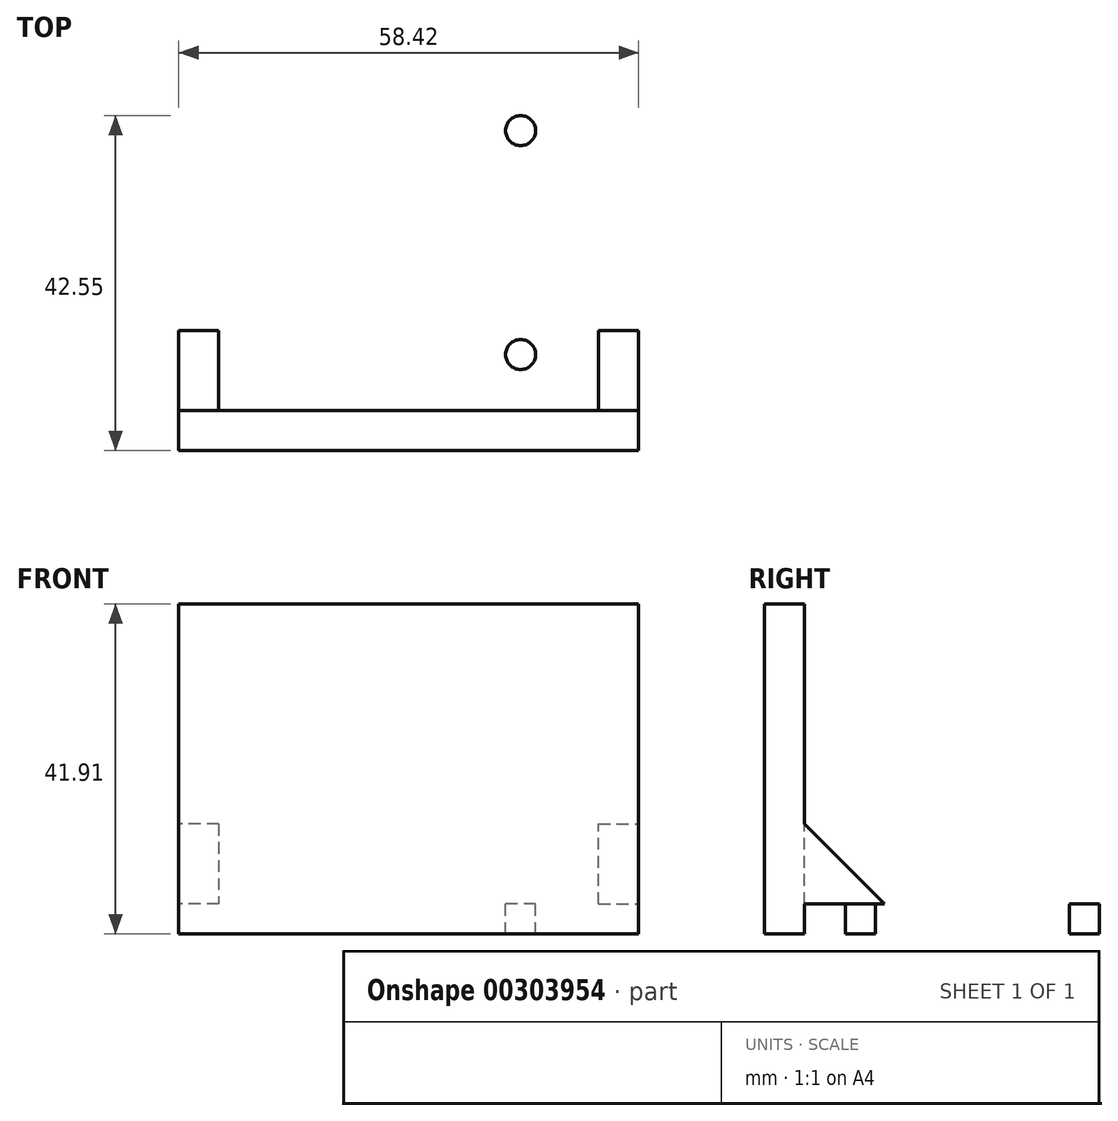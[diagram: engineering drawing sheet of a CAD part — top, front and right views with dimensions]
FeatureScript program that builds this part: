
annotation { "Feature Type Name" : "Feature", "Feature Type Description" : "" }
export const myFeature = defineFeature(function(context is Context, id is Id, definition is map)
    precondition{}
    {
        {
            var Q0;
            Q0=qCreatedBy(makeId("Top.planeOp"),FACE);
            var sketch = newSketch(context, id + "F0", { "sketchPlane" : qUnion([Q0])});
            skLineSegment(sketch, "E0.bottom", {"start": v(29.21, 22.86) * mm, "end": v(-29.21, 22.86) * mm});
            skLineSegment(sketch, "E0.top", {"start": v(29.21, -22.86) * mm, "end": v(-29.21, -22.86) * mm});
            skLineSegment(sketch, "E0.left", {"start": v(29.21, 22.86) * mm, "end": v(29.21, -22.86) * mm});
            skLineSegment(sketch, "E0.right", {"start": v(-29.21, 22.86) * mm, "end": v(-29.21, -22.86) * mm});
            skPoint(sketch, "E0.middle", {"position": v(0, 0) * mm});
            skSolve(sketch);
        }
        {
            var Q0;
            Q0 = qSketchRegion(id + "F0", true);
            extrude(context, id + "F1", {"entities" : qUnion([Q0]), "depth" : 3.8 * mm});
        }
        {
            var Q0;
            Q0=makeQuery(id+"F1.opExtrude","CAP_FACE",FACE,{"disambiguationData":[OSD([sQuery(id+"F0.wireOp",EDGE,"E0.bottom"),sQuery(id+"F0.wireOp",EDGE,"E0.top"),sQuery(id+"F0.wireOp",EDGE,"E0.left"),sQuery(id+"F0.wireOp",EDGE,"E0.right")])],"isStart":false});
            var sketch = newSketch(context, id + "F2", { "sketchPlane" : qUnion([Q0])});
            skLineSegment(sketch, "E1.bottom", {"start": v(-29.21, -22.86) * mm, "end": v(29.21, -22.86) * mm});
            skLineSegment(sketch, "E1.top", {"start": v(-29.21, -17.78) * mm, "end": v(29.21, -17.78) * mm});
            skLineSegment(sketch, "E1.left", {"start": v(-29.21, -22.86) * mm, "end": v(-29.21, -17.78) * mm});
            skLineSegment(sketch, "E1.right", {"start": v(29.21, -22.86) * mm, "end": v(29.21, -17.78) * mm});
            skSolve(sketch);
        }
        {
            var Q0;
            Q0 = qSketchRegion(id + "F2", true);
            extrude(context, id + "F3", {"entities" : qUnion([Q0]), "operationType" : NewBodyOperationType.ADD, "depth" : 38.1 * mm});
        }
        {
            var Q0;
            Q0=makeQuery(id+"F1.opExtrude","CAP_FACE",FACE,{"disambiguationData":[OSD([sQuery(id+"F0.wireOp",EDGE,"E0.bottom"),sQuery(id+"F0.wireOp",EDGE,"E0.top"),sQuery(id+"F0.wireOp",EDGE,"E0.left"),sQuery(id+"F0.wireOp",EDGE,"E0.right")])],"isStart":false});
            var sketch = newSketch(context, id + "F4", { "sketchPlane" : qUnion([Q0])});
            skCircle(sketch, "E2", {"center": v(-14.22, 17.78) * mm, "radius": 1.9 * mm});
            skCircle(sketch, "E3.MirrorC", {"center": v(14.22, 17.78) * mm, "radius": 1.9 * mm});
            skCircle(sketch, "E4", {"center": v(-14.22, -10.67) * mm, "radius": 1.9 * mm});
            skCircle(sketch, "E5.MirrorC", {"center": v(14.22, -10.67) * mm, "radius": 1.9 * mm});
            skSolve(sketch);
        }
        {
            var Q0;
            Q0=makeQuery(id+"F4.imprint","IMPRINT",FACE,{"disambiguationData":[TD([[makeQuery(id+"F4.imprint","IMPRINT",EDGE,{"derivedFrom":sQuery(id+"F4.wireOp",EDGE,"E2")}),1.0]])]});
            var Q1;
            Q1=makeQuery(id+"F4.imprint","IMPRINT",FACE,{"disambiguationData":[TD([[makeQuery(id+"F4.imprint","IMPRINT",EDGE,{"derivedFrom":sQuery(id+"F4.wireOp",EDGE,"E3.MirrorC")}),-1.0]])]});
            var Q2;
            Q2=makeQuery(id+"F4.imprint","IMPRINT",FACE,{"disambiguationData":[TD([[makeQuery(id+"F4.imprint","IMPRINT",EDGE,{"derivedFrom":sQuery(id+"F4.wireOp",EDGE,"E5.MirrorC")}),-1.0]])]});
            var Q3;
            Q3=makeQuery(id+"F4.imprint","IMPRINT",FACE,{"disambiguationData":[TD([[makeQuery(id+"F4.imprint","IMPRINT",EDGE,{"derivedFrom":sQuery(id+"F4.wireOp",EDGE,"E4")}),1.0]])]});
            extrude(context, id + "F5", {"entities" : qUnion([Q0, Q1, Q2, Q3]), "operationType" : NewBodyOperationType.REMOVE, "endBound" : BoundingType.THROUGH_ALL, "oppositeDirection" : true, "depth" : 25.4 * mm});
        }
        {
            var Q0;
            Q0=makeQuery(id+"F3.boolean.opBoolean","MERGE",FACE,{"derivedFrom":[makeQuery(id+"F1.opExtrude","SWEPT_FACE",FACE,{"disambiguationData":[OSD([sQuery(id+"F0.wireOp",EDGE,"E0.right")])]}),makeQuery(id+"F3.opExtrude","SWEPT_FACE",FACE,{"disambiguationData":[OSD([sQuery(id+"F2.wireOp",EDGE,"E1.left")])]})]});
            var sketch = newSketch(context, id + "F6", { "sketchPlane" : qUnion([Q0])});
            skLineSegment(sketch, "E6.bottom", {"start": v(17.78, 3.81) * mm, "end": v(7.62, 3.81) * mm});
            skLineSegment(sketch, "E6.top", {"start": v(17.78, 13.97) * mm, "end": v(7.62, 13.97) * mm});
            skLineSegment(sketch, "E6.left", {"start": v(17.78, 3.81) * mm, "end": v(17.78, 13.97) * mm});
            skLineSegment(sketch, "E6.right", {"start": v(7.62, 3.81) * mm, "end": v(7.62, 13.97) * mm});
            skSolve(sketch);
        }
        {
            var Q0;
            Q0 = qSketchRegion(id + "F6", true);
            extrude(context, id + "F7", {"entities" : qUnion([Q0]), "operationType" : NewBodyOperationType.ADD, "oppositeDirection" : true, "depth" : 5.08 * mm});
        }
        {
            var Q0;
            Q0=makeQuery(id+"F7.opExtrude","SWEPT_EDGE",EDGE,{"disambiguationData":[OSD([sQuery(id+"F6.wireOp",EDGE,"E6.top"),sQuery(id+"F6.wireOp",EDGE,"E6.right")])]});
            chamfer(context, id + "F8", {"entities" : qUnion([Q0]), "width" : 10.16 * mm, "tangentPropagation" : true});
        }
        {
            var Q0;
            Q0=makeQuery(id+"F3.boolean.opBoolean","MERGE",FACE,{"derivedFrom":[makeQuery(id+"F1.opExtrude","SWEPT_FACE",FACE,{"disambiguationData":[OSD([sQuery(id+"F0.wireOp",EDGE,"E0.left")])]}),makeQuery(id+"F3.opExtrude","SWEPT_FACE",FACE,{"disambiguationData":[OSD([sQuery(id+"F2.wireOp",EDGE,"E1.right")])]})]});
            var sketch = newSketch(context, id + "F9", { "sketchPlane" : qUnion([Q0])});
            skLineSegment(sketch, "E7.bottom", {"start": v(-17.78, 3.81) * mm, "end": v(-7.62, 3.81) * mm});
            skLineSegment(sketch, "E7.top", {"start": v(-17.78, 13.97) * mm, "end": v(-7.62, 13.97) * mm});
            skLineSegment(sketch, "E7.left", {"start": v(-17.78, 3.81) * mm, "end": v(-17.78, 13.97) * mm});
            skLineSegment(sketch, "E7.right", {"start": v(-7.62, 3.81) * mm, "end": v(-7.62, 13.97) * mm});
            skSolve(sketch);
        }
        {
            var Q0;
            Q0 = qSketchRegion(id + "F9", true);
            extrude(context, id + "F10", {"entities" : qUnion([Q0]), "operationType" : NewBodyOperationType.ADD, "oppositeDirection" : true, "depth" : 5.08 * mm});
        }
        {
            var Q0;
            Q0=makeQuery(id+"F10.opExtrude","SWEPT_EDGE",EDGE,{"disambiguationData":[OSD([sQuery(id+"F9.wireOp",EDGE,"E7.top"),sQuery(id+"F9.wireOp",EDGE,"E7.right")])]});
            chamfer(context, id + "F11", {"entities" : qUnion([Q0]), "width" : 10.16 * mm, "tangentPropagation" : true});
        }
    });
